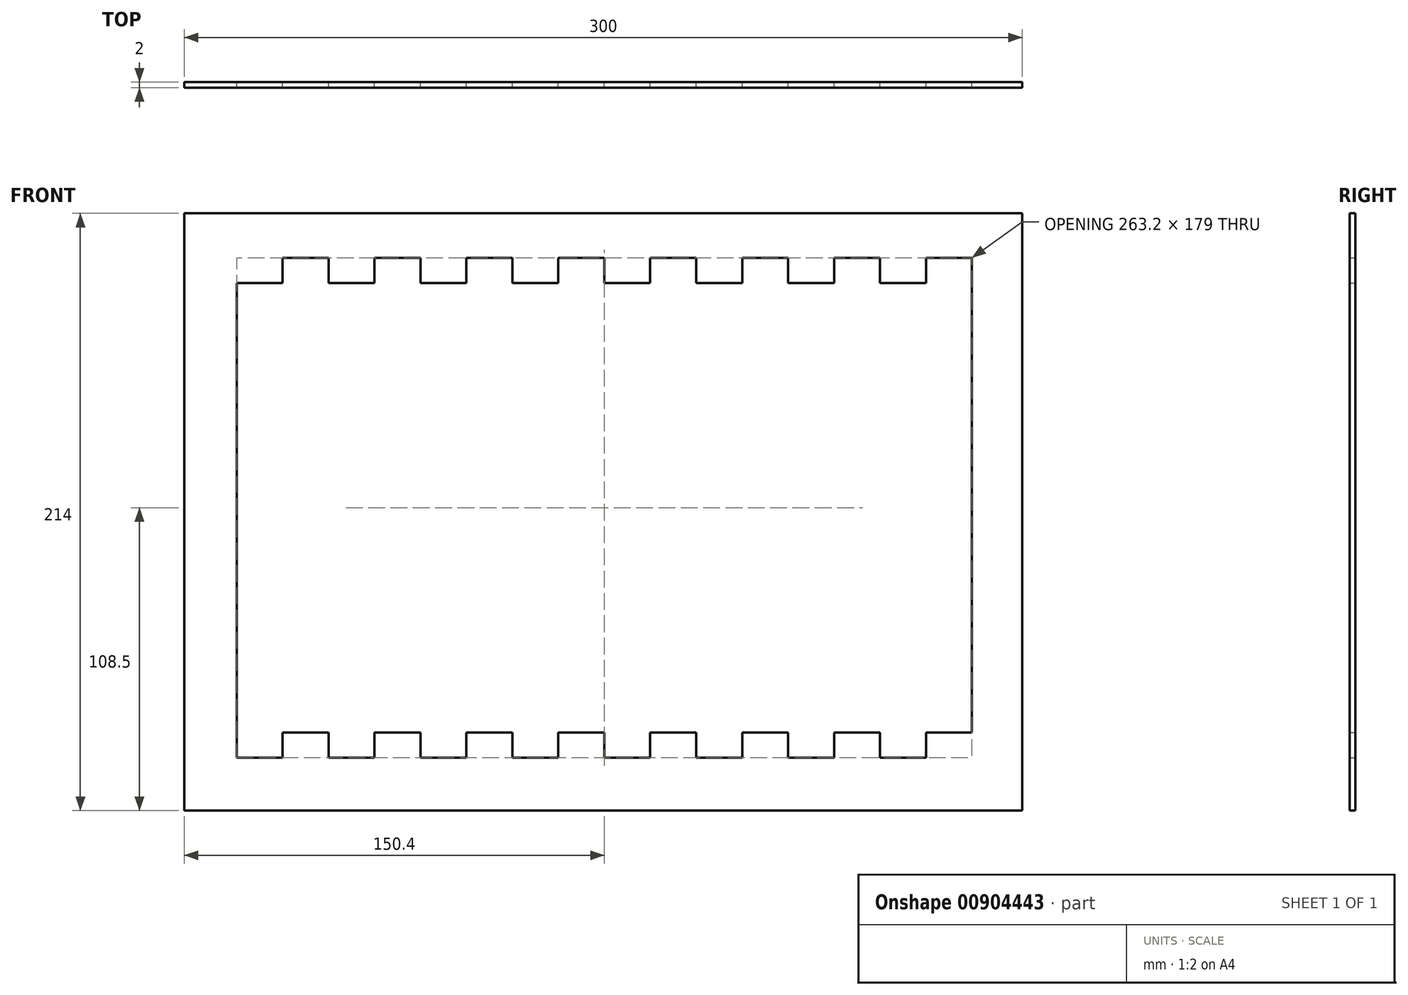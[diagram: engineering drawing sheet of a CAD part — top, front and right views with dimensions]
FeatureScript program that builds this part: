
annotation { "Feature Type Name" : "Feature", "Feature Type Description" : "" }
export const myFeature = defineFeature(function(context is Context, id is Id, definition is map)
    precondition{}
    {
        {
            var Q0;
            Q0=qCreatedBy(makeId("Front.planeOp"),FACE);
            var sketch = newSketch(context, id + "F0", { "sketchPlane" : qUnion([Q0])});
            skLineSegment(sketch, "E0", {"start": v(0, 0) * mm, "end": v(-16.45, 0) * mm});
            skLineSegment(sketch, "E1", {"start": v(-16.45, 0) * mm, "end": v(-16.45, -9) * mm});
            skLineSegment(sketch, "E2", {"start": v(-16.45, -9) * mm, "end": v(-32.9, -9) * mm});
            skLineSegment(sketch, "E3", {"start": v(-32.9, -9) * mm, "end": v(-32.9, 0) * mm});
            skLineSegment(sketch, "E4.0.1.0", {"start": v(-32.9, 161) * mm, "end": v(-32.9, 170) * mm});
            skLineSegment(sketch, "E4.0.1.1", {"start": v(-16.45, 161) * mm, "end": v(-32.9, 161) * mm});
            skLineSegment(sketch, "E4.0.1.2", {"start": v(0, 170) * mm, "end": v(-16.45, 170) * mm});
            skLineSegment(sketch, "E4.0.1.3", {"start": v(-16.45, 170) * mm, "end": v(-16.45, 161) * mm});
            skLineSegment(sketch, "E4.1.0.0", {"start": v(-65.8, -9) * mm, "end": v(-65.8, 0) * mm});
            skLineSegment(sketch, "E4.1.0.1", {"start": v(-49.35, -9) * mm, "end": v(-65.8, -9) * mm});
            skLineSegment(sketch, "E4.1.0.2", {"start": v(-32.9, 0) * mm, "end": v(-49.35, 0) * mm});
            skLineSegment(sketch, "E4.1.0.3", {"start": v(-49.35, 0) * mm, "end": v(-49.35, -9) * mm});
            skLineSegment(sketch, "E4.1.1.0", {"start": v(-65.8, 161) * mm, "end": v(-65.8, 170) * mm});
            skLineSegment(sketch, "E4.1.1.1", {"start": v(-49.35, 161) * mm, "end": v(-65.8, 161) * mm});
            skLineSegment(sketch, "E4.1.1.2", {"start": v(-32.9, 170) * mm, "end": v(-49.35, 170) * mm});
            skLineSegment(sketch, "E4.1.1.3", {"start": v(-49.35, 170) * mm, "end": v(-49.35, 161) * mm});
            skLineSegment(sketch, "E4.2.0.0", {"start": v(-98.7, -9) * mm, "end": v(-98.7, 0) * mm});
            skLineSegment(sketch, "E4.2.0.1", {"start": v(-82.25, -9) * mm, "end": v(-98.7, -9) * mm});
            skLineSegment(sketch, "E4.2.0.2", {"start": v(-65.8, 0) * mm, "end": v(-82.25, 0) * mm});
            skLineSegment(sketch, "E4.2.0.3", {"start": v(-82.25, 0) * mm, "end": v(-82.25, -9) * mm});
            skLineSegment(sketch, "E4.2.1.0", {"start": v(-98.7, 161) * mm, "end": v(-98.7, 170) * mm});
            skLineSegment(sketch, "E4.2.1.1", {"start": v(-82.25, 161) * mm, "end": v(-98.7, 161) * mm});
            skLineSegment(sketch, "E4.2.1.2", {"start": v(-65.8, 170) * mm, "end": v(-82.25, 170) * mm});
            skLineSegment(sketch, "E4.2.1.3", {"start": v(-82.25, 170) * mm, "end": v(-82.25, 161) * mm});
            skLineSegment(sketch, "E4.3.0.0", {"start": v(-131.6, -9) * mm, "end": v(-131.6, 0) * mm});
            skLineSegment(sketch, "E4.3.0.1", {"start": v(-115.15, -9) * mm, "end": v(-131.6, -9) * mm});
            skLineSegment(sketch, "E4.3.0.2", {"start": v(-98.7, 0) * mm, "end": v(-115.15, 0) * mm});
            skLineSegment(sketch, "E4.3.0.3", {"start": v(-115.15, 0) * mm, "end": v(-115.15, -9) * mm});
            skLineSegment(sketch, "E4.3.1.0", {"start": v(-131.6, 161) * mm, "end": v(-131.6, 170) * mm});
            skLineSegment(sketch, "E4.3.1.1", {"start": v(-115.15, 161) * mm, "end": v(-131.6, 161) * mm});
            skLineSegment(sketch, "E4.3.1.2", {"start": v(-98.7, 170) * mm, "end": v(-115.15, 170) * mm});
            skLineSegment(sketch, "E4.3.1.3", {"start": v(-115.15, 170) * mm, "end": v(-115.15, 161) * mm});
            skLineSegment(sketch, "E4.4.0.0", {"start": v(-164.5, -9) * mm, "end": v(-164.5, 0) * mm});
            skLineSegment(sketch, "E4.4.0.1", {"start": v(-148.05, -9) * mm, "end": v(-164.5, -9) * mm});
            skLineSegment(sketch, "E4.4.0.2", {"start": v(-131.6, 0) * mm, "end": v(-148.05, 0) * mm});
            skLineSegment(sketch, "E4.4.0.3", {"start": v(-148.05, 0) * mm, "end": v(-148.05, -9) * mm});
            skLineSegment(sketch, "E4.4.1.0", {"start": v(-164.5, 161) * mm, "end": v(-164.5, 170) * mm});
            skLineSegment(sketch, "E4.4.1.1", {"start": v(-148.05, 161) * mm, "end": v(-164.5, 161) * mm});
            skLineSegment(sketch, "E4.4.1.2", {"start": v(-131.6, 170) * mm, "end": v(-148.05, 170) * mm});
            skLineSegment(sketch, "E4.4.1.3", {"start": v(-148.05, 170) * mm, "end": v(-148.05, 161) * mm});
            skLineSegment(sketch, "E4.5.0.0", {"start": v(-197.4, -9) * mm, "end": v(-197.4, 0) * mm});
            skLineSegment(sketch, "E4.5.0.1", {"start": v(-180.95, -9) * mm, "end": v(-197.4, -9) * mm});
            skLineSegment(sketch, "E4.5.0.2", {"start": v(-164.5, 0) * mm, "end": v(-180.95, 0) * mm});
            skLineSegment(sketch, "E4.5.0.3", {"start": v(-180.95, 0) * mm, "end": v(-180.95, -9) * mm});
            skLineSegment(sketch, "E4.5.1.0", {"start": v(-197.4, 161) * mm, "end": v(-197.4, 170) * mm});
            skLineSegment(sketch, "E4.5.1.1", {"start": v(-180.95, 161) * mm, "end": v(-197.4, 161) * mm});
            skLineSegment(sketch, "E4.5.1.2", {"start": v(-164.5, 170) * mm, "end": v(-180.95, 170) * mm});
            skLineSegment(sketch, "E4.5.1.3", {"start": v(-180.95, 170) * mm, "end": v(-180.95, 161) * mm});
            skLineSegment(sketch, "E4.6.0.0", {"start": v(-230.3, -9) * mm, "end": v(-230.3, 0) * mm});
            skLineSegment(sketch, "E4.6.0.1", {"start": v(-213.85, -9) * mm, "end": v(-230.3, -9) * mm});
            skLineSegment(sketch, "E4.6.0.2", {"start": v(-197.4, 0) * mm, "end": v(-213.85, 0) * mm});
            skLineSegment(sketch, "E4.6.0.3", {"start": v(-213.85, 0) * mm, "end": v(-213.85, -9) * mm});
            skLineSegment(sketch, "E4.6.1.0", {"start": v(-230.3, 161) * mm, "end": v(-230.3, 170) * mm});
            skLineSegment(sketch, "E4.6.1.1", {"start": v(-213.85, 161) * mm, "end": v(-230.3, 161) * mm});
            skLineSegment(sketch, "E4.6.1.2", {"start": v(-197.4, 170) * mm, "end": v(-213.85, 170) * mm});
            skLineSegment(sketch, "E4.6.1.3", {"start": v(-213.85, 170) * mm, "end": v(-213.85, 161) * mm});
            skLineSegment(sketch, "E4.7.0.0", {"start": v(-263.2, -9) * mm, "end": v(-263.2, 0) * mm});
            skLineSegment(sketch, "E4.7.0.1", {"start": v(-246.75, -9) * mm, "end": v(-263.2, -9) * mm});
            skLineSegment(sketch, "E4.7.0.2", {"start": v(-230.3, 0) * mm, "end": v(-246.75, 0) * mm});
            skLineSegment(sketch, "E4.7.0.3", {"start": v(-246.75, 0) * mm, "end": v(-246.75, -9) * mm});
            skLineSegment(sketch, "E4.7.1.1", {"start": v(-246.75, 161) * mm, "end": v(-263.2, 161) * mm});
            skLineSegment(sketch, "E4.7.1.2", {"start": v(-230.3, 170) * mm, "end": v(-246.75, 170) * mm});
            skLineSegment(sketch, "E4.7.1.3", {"start": v(-246.75, 170) * mm, "end": v(-246.75, 161) * mm});
            skLineSegment(sketch, "E4.direction1", {"start": v(-32.9, -9) * mm, "end": v(-65.8, -9) * mm, "construction": true});
            skLineSegment(sketch, "E4.direction2", {"start": v(-32.9, -9) * mm, "end": v(-32.9, 161) * mm, "construction": true});
            skLineSegment(sketch, "E5", {"start": v(0, 170) * mm, "end": v(0, 0) * mm});
            skLineSegment(sketch, "E6.bottom", {"start": v(18, -28) * mm, "end": v(-282, -28) * mm});
            skLineSegment(sketch, "E6.top", {"start": v(18, 186) * mm, "end": v(-282, 186) * mm});
            skLineSegment(sketch, "E6.left", {"start": v(18, -28) * mm, "end": v(18, 186) * mm});
            skLineSegment(sketch, "E6.right", {"start": v(-282, -28) * mm, "end": v(-282, 186) * mm});
            skLineSegment(sketch, "E7", {"start": v(-263.2, 0) * mm, "end": v(-263.2, 161) * mm});
            skSolve(sketch);
        }
        {
            var Q0;
            Q0=makeQuery(id+"F0.imprint","IMPRINT",FACE,{"disambiguationData":[TD([[makeQuery(id+"F0.imprint","IMPRINT",EDGE,{"derivedFrom":sQuery(id+"F0.wireOp",EDGE,"E0")}),1.0]])]});
            extrude(context, id + "F1", {"entities" : qUnion([Q0]), "depth" : 2 * mm, "offsetDistance" : 25 * mm});
        }
    });
